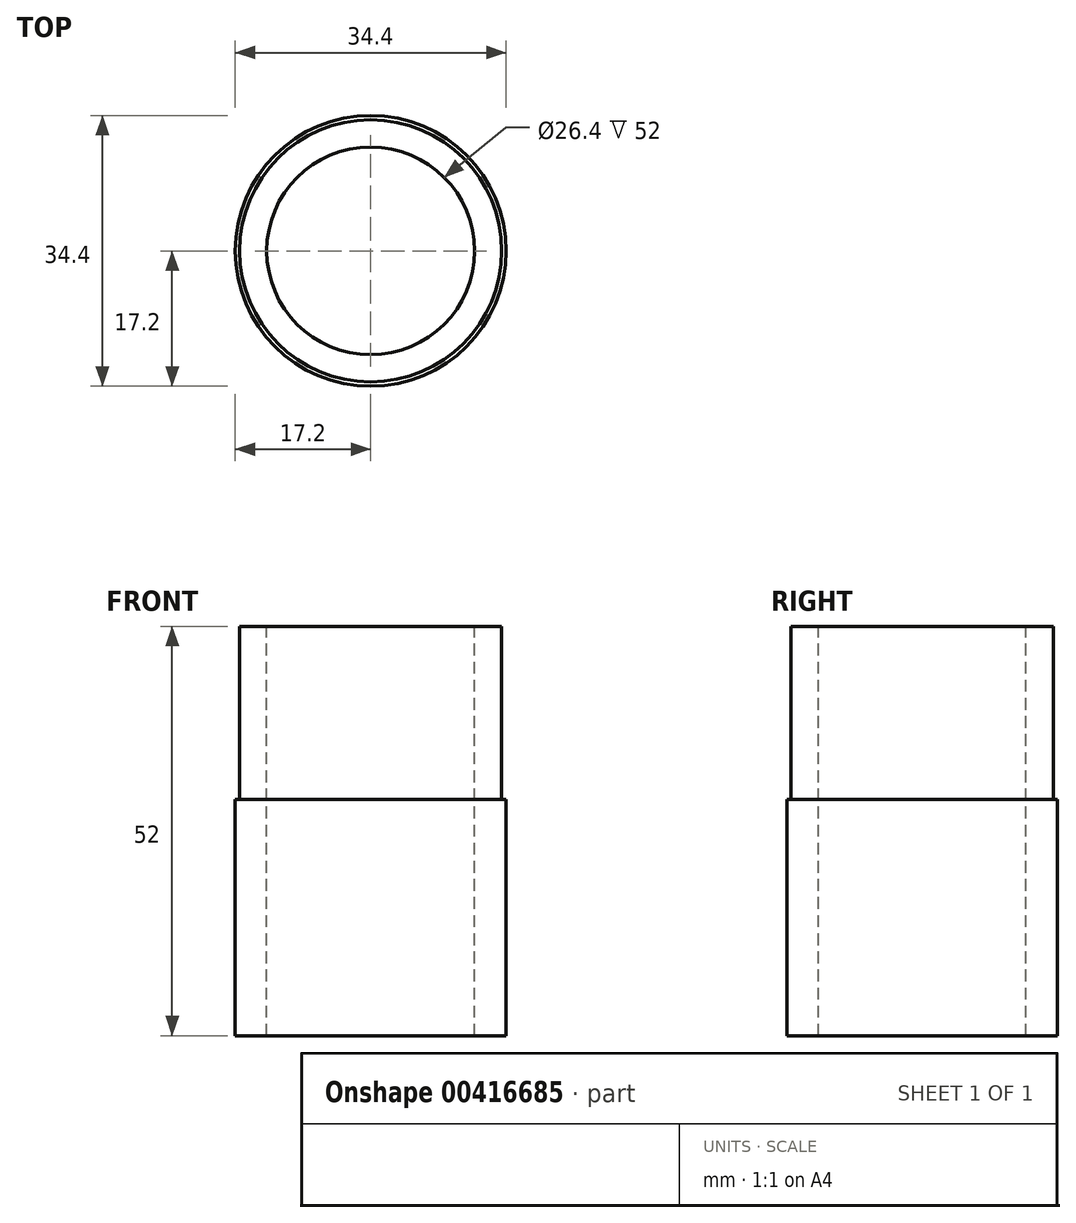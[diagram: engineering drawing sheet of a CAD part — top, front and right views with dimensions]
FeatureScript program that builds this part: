
annotation { "Feature Type Name" : "Feature", "Feature Type Description" : "" }
export const myFeature = defineFeature(function(context is Context, id is Id, definition is map)
    precondition{}
    {
        {
            var Q0;
            Q0=qCreatedBy(makeId("Top.planeOp"),FACE);
            var sketch = newSketch(context, id + "F0", { "sketchPlane" : qUnion([Q0])});
            skCircle(sketch, "E0", {"center": v(0, 0) * mm, "radius": 17.2 * mm});
            skSolve(sketch);
        }
        {
            var Q0;
            Q0=makeQuery(id+"F0.imprint","IMPRINT",FACE,{"disambiguationData":[TD([[makeQuery(id+"F0.imprint","IMPRINT",EDGE,{"derivedFrom":sQuery(id+"F0.wireOp",EDGE,"E0")}),1.0]])]});
            extrude(context, id + "F1", {"entities" : qUnion([Q0]), "depth" : 30 * mm});
        }
        {
            var Q0;
            Q0=makeQuery(id+"F1.opExtrude","CAP_FACE",FACE,{"disambiguationData":[OSD([sQuery(id+"F0.wireOp",EDGE,"E0")])],"isStart":false});
            var sketch = newSketch(context, id + "F2", { "sketchPlane" : qUnion([Q0])});
            skCircle(sketch, "E1", {"center": v(0, 0) * mm, "radius": 16.65 * mm});
            skSolve(sketch);
        }
        {
            var Q0;
            Q0=makeQuery(id+"F2.imprint","IMPRINT",FACE,{"disambiguationData":[TD([[makeQuery(id+"F2.imprint","IMPRINT",EDGE,{"derivedFrom":sQuery(id+"F2.wireOp",EDGE,"E1")}),1.0]])]});
            extrude(context, id + "F3", {"entities" : qUnion([Q0]), "operationType" : NewBodyOperationType.ADD, "depth" : 22 * mm});
        }
        {
            var Q0;
            Q0=makeQuery(id+"F3.opExtrude","CAP_FACE",FACE,{"disambiguationData":[OSD([sQuery(id+"F2.wireOp",EDGE,"E1")])],"isStart":false});
            var sketch = newSketch(context, id + "F4", { "sketchPlane" : qUnion([Q0])});
            skCircle(sketch, "E2", {"center": v(0, 0) * mm, "radius": 13.2 * mm});
            skSolve(sketch);
        }
        {
            var Q0;
            Q0=makeQuery(id+"F4.imprint","IMPRINT",FACE,{"disambiguationData":[TD([[makeQuery(id+"F4.imprint","IMPRINT",EDGE,{"derivedFrom":sQuery(id+"F4.wireOp",EDGE,"E2")}),1.0]])]});
            extrude(context, id + "F5", {"entities" : qUnion([Q0]), "operationType" : NewBodyOperationType.REMOVE, "oppositeDirection" : true, "depth" : 25 * mm});
        }
        {
            var Q0;
            Q0=makeQuery(id+"F1.opExtrude","CAP_FACE",FACE,{"disambiguationData":[OSD([sQuery(id+"F0.wireOp",EDGE,"E0")])],"isStart":true});
            var sketch = newSketch(context, id + "F6", { "sketchPlane" : qUnion([Q0])});
            skCircle(sketch, "E3", {"center": v(0, 0) * mm, "radius": 13.2 * mm});
            skSolve(sketch);
        }
        {
            var Q0;
            Q0=makeQuery(id+"F6.imprint","IMPRINT",FACE,{"disambiguationData":[TD([[makeQuery(id+"F6.imprint","IMPRINT",EDGE,{"derivedFrom":sQuery(id+"F6.wireOp",EDGE,"E3")}),1.0]])]});
            extrude(context, id + "F7", {"entities" : qUnion([Q0]), "operationType" : NewBodyOperationType.REMOVE, "oppositeDirection" : true, "depth" : 30 * mm});
        }
    });
